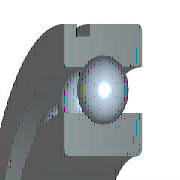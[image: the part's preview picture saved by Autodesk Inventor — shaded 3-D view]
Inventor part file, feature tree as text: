
AUTODESK INVENTOR PART (.ipt)
format: ipt  version: 2015 (Build 190159000, 159)  size: 319,488 bytes
history: native  units: mm (DEFAULTED — no unit token found)
features: sketch x1, other x1, pattern_circular x1
ambient origin geometry x8: Origin, YZ Plane, XZ Plane, XY Plane, X Axis, Y Axis, Z Axis, Center Point
bodies: Solid1 (feature_tree)
feature tree (3):
  sketch  "草图"  dims[d0=4.68mm d17=90.0deg d18=90.0deg d1=0.3mm d2=90.0mm d3=360.0deg d4=0.0mm d5=0.0mm d6=0.0mm d7=17.0mm d8=35.0mm d9=26.0mm d10=33.92mm d11=22.868mm d12=22.868mm d13=22.868mm d14=0.0mm d15=10.0mm d16=10.0mm d19=1.666667mm d20=3.333333mm d22=5.0mm d23=0.0mm d24=0.0mm]
  other  "轴承体"
  pattern_circular  "IDS_ARRAYBALL[SIMPL:T]"  Angle=90.0deg  [1 undecoded]
note: 1 required parameter value undecoded (feature->parameter linkage not recoverable at this tier; creation-order binding heuristic only, values carry confidence <= 0.55)
